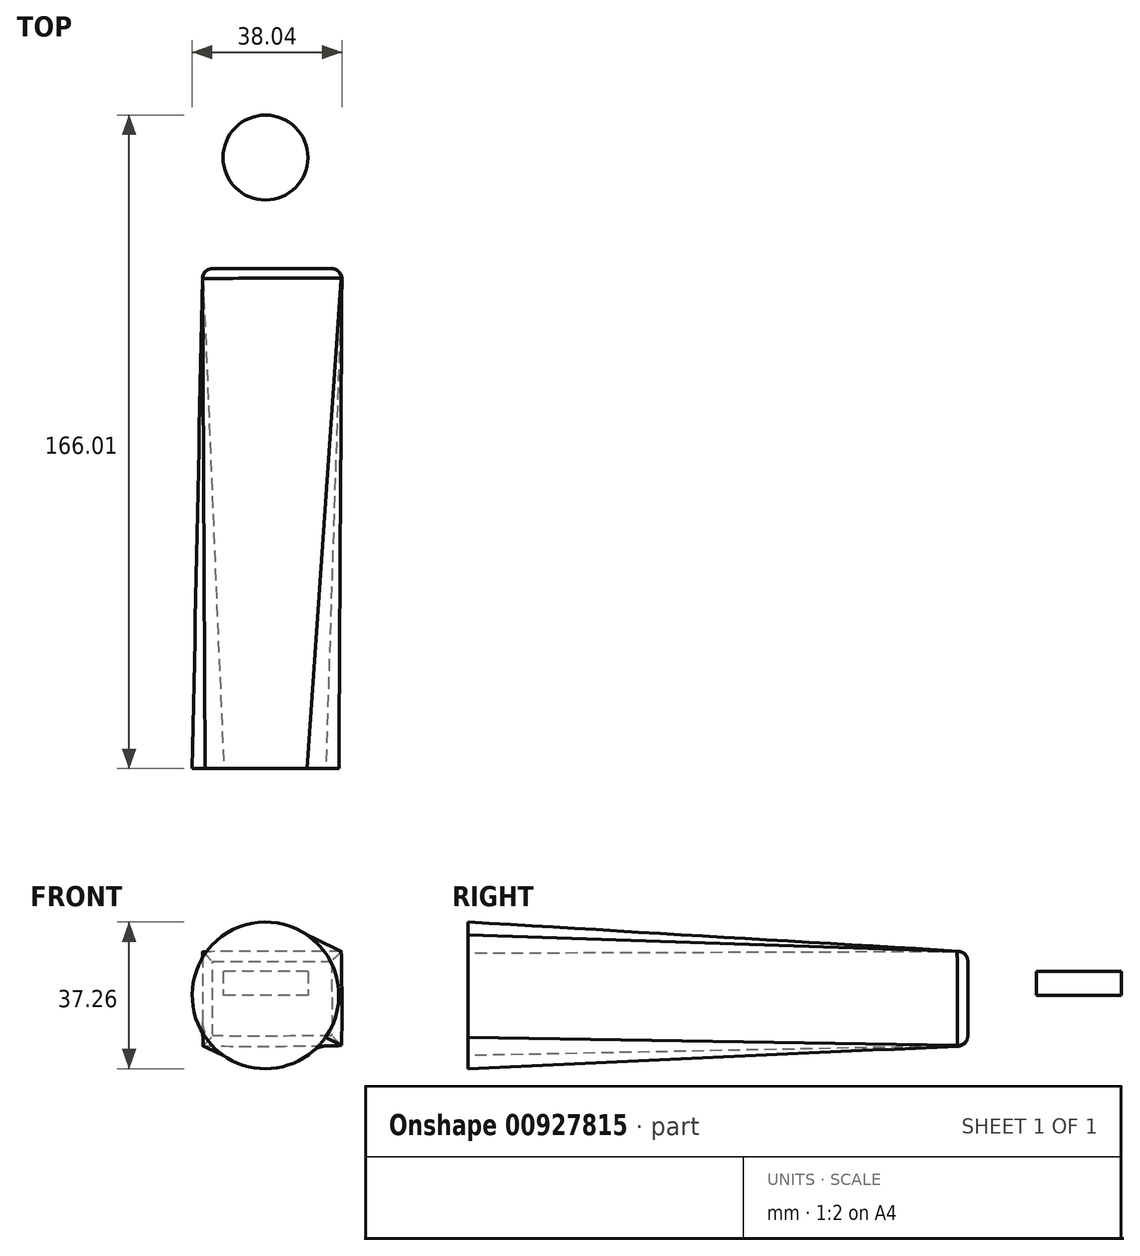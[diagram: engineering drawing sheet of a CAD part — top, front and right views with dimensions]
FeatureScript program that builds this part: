
annotation { "Feature Type Name" : "Feature", "Feature Type Description" : "" }
export const myFeature = defineFeature(function(context is Context, id is Id, definition is map)
    precondition{}
    {
        {
            var Q0;
            Q0=qCreatedBy(makeId("Front.planeOp"),FACE);
            var sketch = newSketch(context, id + "F0", { "sketchPlane" : qUnion([Q0])});
            skLineSegment(sketch, "E0.bottom", {"start": v(-15.97, 11.08) * mm, "end": v(19.43, 11.08) * mm});
            skLineSegment(sketch, "E0.top", {"start": v(-15.97, -12.8) * mm, "end": v(19.43, -12.8) * mm});
            skLineSegment(sketch, "E0.left", {"start": v(-15.97, 11.08) * mm, "end": v(-15.97, -12.8) * mm});
            skLineSegment(sketch, "E0.right", {"start": v(19.43, 11.08) * mm, "end": v(19.43, -12.8) * mm});
            skSolve(sketch);
        }
        {
            var Q0;
            Q0=qCreatedBy(makeId("Front.planeOp"),FACE);
            cPlane(context, id + "F1", {"entities" : qUnion([Q0]), "cplaneType" : CPlaneType.OFFSET, "offset" : 127 * mm, "width" : 152.4 * mm, "height" : 152.4 * mm});
        }
        {
            var Q0;
            Q0=qCreatedBy(id+"F1.planeOp",FACE);
            var sketch = newSketch(context, id + "F2", { "sketchPlane" : qUnion([Q0])});
            skCircle(sketch, "E1", {"center": v(0, 0) * mm, "radius": 18.63 * mm});
            skSolve(sketch);
        }
        {
            var Q0;
            Q0=makeQuery(id+"F0.imprint","IMPRINT",FACE,{"disambiguationData":[TD([[makeQuery(id+"F0.imprint","IMPRINT",EDGE,{"derivedFrom":sQuery(id+"F0.wireOp",EDGE,"E0.bottom")}),-1.0]])]});
            var Q1;
            Q1=makeQuery(id+"F2.imprint","IMPRINT",FACE,{"disambiguationData":[TD([[makeQuery(id+"F2.imprint","IMPRINT",EDGE,{"derivedFrom":sQuery(id+"F2.wireOp",EDGE,"E1")}),1.0]])]});
            loft(context, id + "F3", {"sheetProfilesArray" : [{ "sheetProfileEntities" : qUnion([Q0]) }, { "sheetProfileEntities" : qUnion([Q1]) }]});
        }
        {
            var Q0;
            Q0=makeQuery(id+"F3.opLoft","CAP_FACE",FACE,{"disambiguationData":[OSD([makeQuery(id+"F0.imprint","IMPRINT",FACE,{"disambiguationData":[TD([[makeQuery(id+"F0.imprint","IMPRINT",EDGE,{"derivedFrom":sQuery(id+"F0.wireOp",EDGE,"E0.bottom")}),-1.0]])]})])],"isStart":true});
            fillet(context, id + "F4", {"entities" : qUnion([Q0]), "radius" : 2.54 * mm, "tangentPropagation" : true, "allowEdgeOverflow" : false});
        }
        {
            var Q0;
            Q0=qCreatedBy(makeId("Top.planeOp"),FACE);
            var sketch = newSketch(context, id + "F5", { "sketchPlane" : qUnion([Q0])});
            skCircle(sketch, "E2", {"center": v(0, 28.22) * mm, "radius": 10.79 * mm});
            skSolve(sketch);
        }
        {
            var Q0;
            Q0=makeQuery(id+"F5.imprint","IMPRINT",FACE,{"disambiguationData":[TD([[makeQuery(id+"F5.imprint","IMPRINT",EDGE,{"derivedFrom":sQuery(id+"F5.wireOp",EDGE,"E2")}),1.0]])]});
            extrude(context, id + "F6", {"entities" : qUnion([Q0]), "depth" : 6.1 * mm, "offsetDistance" : 25.4 * mm});
        }
    });
